# Revit family: ElectricalFixture_WiringAccessories_Hager_Sollysta_50ADoublePoleSwitches
name_source: partatom
category: Electrical Fixtures
revit_build: Autodesk Revit 2015 (Build: 20160512_1515(x64)
units: mm (PartAtom-declared; Revit-internal decimal feet)

## types (9) — shared parameters
CE Approval = Yes
Colour = SollystaWhite
Default Elevation = 1219.2 mm  [stored 4 ft]
Design Country = China
Distance From Centre = 22.4 mm
Distance From Edge = 63.6 mm
Expected Life = 25 years
Extrusion From Wall = 12.6 mm
Finish = Gloss
Frequency = 50/60Hz
Gross Weight kg = 0.165
LED Indicator Switch = Yes
Manufacturer = Hager
Manufacturer Country = United Kingdom
Manufacturer Website = http://www.hager.co.uk
Material = Urea Formaldehyde Thermoset Plastic
Overall Depth = 26.1 mm
Overall Length = 86 mm  [stored 0.282152 ft]
Packaging Recyclable = Yes
Product Group = WiringAccessories
Product Literature = http://www.hager.co.uk
Product Range = Sollysta
Product URL = http://www.hager.co.uk
Reference Standard = BS 1363-2
Shape = Rectangular
Shipping Weight kg = 0.188
Supply Phase = 1
Switch = Yes
Type = ElectricalFixture
Voltage (Volts) = 230V/240V
zero-valued in all types: Overall Width

## per-type parameters (varying)
| type | Description | Double | EAN Code | Features | Name | Overall Height | Product Family | Single | Technical Description |
| WMDP50N | 50ADoublePoleSwitch1GangwithLEDIndicator | No | 5015652260325 | 50ADoublePoleSwitch1GangwithLEDIndicator | WhiteMouldedSocket_WMDP50N | 86 mm  [stored 0.282152 ft] | WhiteMouldedSockets_50ADoublePoleSwitches | Yes | 50ADoublePoleSwitch1GangwithLEDIndicator |
| WMDP50N/CK | 50ADoublePoleSwitch1GangwithLEDIndicatorMarkedCooker | No | 5015652260332 | 50ADoublePoleSwitch1GangwithLEDIndicatorMarkedCooker | WhiteMouldedSocket_WMDP50N/CK | 86 mm  [stored 0.282152 ft] | WhiteMoldedSockets | Yes | 50ADoublePoleSwitch1GangwithLEDIndicatorMarkedCooker |
| WMDP50N/HB | 50ADoublePoleSwitch1GangwithLEDIndicatorMarkedHob | No | 5015652260349 | 50ADoublePoleSwitch1GangwithLEDIndicatorMarkedHob | WhiteMouldedSocket_WMDP50N/CK | 86 mm  [stored 0.282152 ft] | WhiteMouldedSockets_50ADoublePoleSwitches | Yes | 50ADoublePoleSwitch1GangwithLEDIndicatorMarkedHob |
| WMDP50N/OV | 50ADoublePoleSwitch1GangwithLEDIndicatorMarkedOven | No | 5015652260356 | 50ADoublePoleSwitch1GangwithLEDIndicatorMarkedOven | WhiteMouldedSocket_WMDP50N/CK | 86 mm  [stored 0.282152 ft] | WhiteMouldedSockets_50ADoublePoleSwitches | Yes | 50ADoublePoleSwitch1GangwithLEDIndicatorMarkedOven |
| WMDP50N/SH | 50ADoublePoleSwitch1GangwithLEDIndicatorMarkedShower | No | 5015652260363 | 50ADoublePoleSwitch1GangwithLEDIndicatorMarkedShower | WhiteMouldedSocket_WMDP50N/SH | 86 mm  [stored 0.282152 ft] | WhiteMouldedSockets_50ADoublePoleSwitches | Yes | 50ADoublePoleSwitch1GangwithLEDIndicatorMarkedShower |
| WMDP50VN | 50ADoublePoleSwitch2GangVerticalwithLEDIndicator | Yes | 5015652260479 | 50ADoublePoleSwitch2GangVerticalwithLEDIndicator | WhiteMouldedSocket_WMDP50VN | 146 mm  [stored 0.479003 ft] | WhiteMouldedSockets_50ADoublePoleSwitches | No | 50ADoublePoleSwitch2GangVerticalwithLEDIndicator |
| WMDP50VN/CK | 50ADoublePoleSwitch2GangVerticalwithLEDIndicatorMarkedCooker | Yes | 5015652260486 | 50ADoublePoleSwitch2GangVerticalwithLEDIndicatorMarkedCooker | WhiteMouldedSocket_WMDP50VN/CK | 146 mm  [stored 0.479003 ft] | WhiteMouldedSockets_50ADoublePoleSwitches | No | 50ADoublePoleSwitch2GangVerticalwithLEDIndicatorMarkedCooker |
| WMDP50VN/HB | 50ADoublePoleSwitch2GangVerticalwithLEDIndicatorMarkedHob | Yes | 5015652260493 | 50ADoublePoleSwitch2GangVerticalwithLEDIndicatorMarkedHob | WhiteMouldedSocket_WMDP50VN/HB | 146 mm  [stored 0.479003 ft] | WhiteMouldedSockets_50ADoublePoleSwitches | No | 50ADoublePoleSwitch2GangVerticalwithLEDIndicatorMarkedHob |
| WMDP50VN/OV | 50ADoublePoleSwitch2GangVerticalwithLEDIndicatorMarkedOven | Yes | 5015652260509 | 50ADoublePoleSwitch2GangVerticalwithLEDIndicatorMarkedOven | WhiteMouldedSocket_WMDP50VN/OV | 146 mm  [stored 0.479003 ft] | WhiteMouldedSockets_50ADoublePoleSwitches | No | 50ADoublePoleSwitch2GangVerticalwithLEDIndicatorMarkedOven |

note: column(s) folded — value = type name in every type: Product Model Number, Unique Reference

note: [stored X ft] marks values corroborated as IEEE doubles in the binary element streams (Revit-internal decimal feet)

## geometry (parser evidence)
native form markers: Blend x4, Sweep x3
no freeform markers — native parametric forms only
